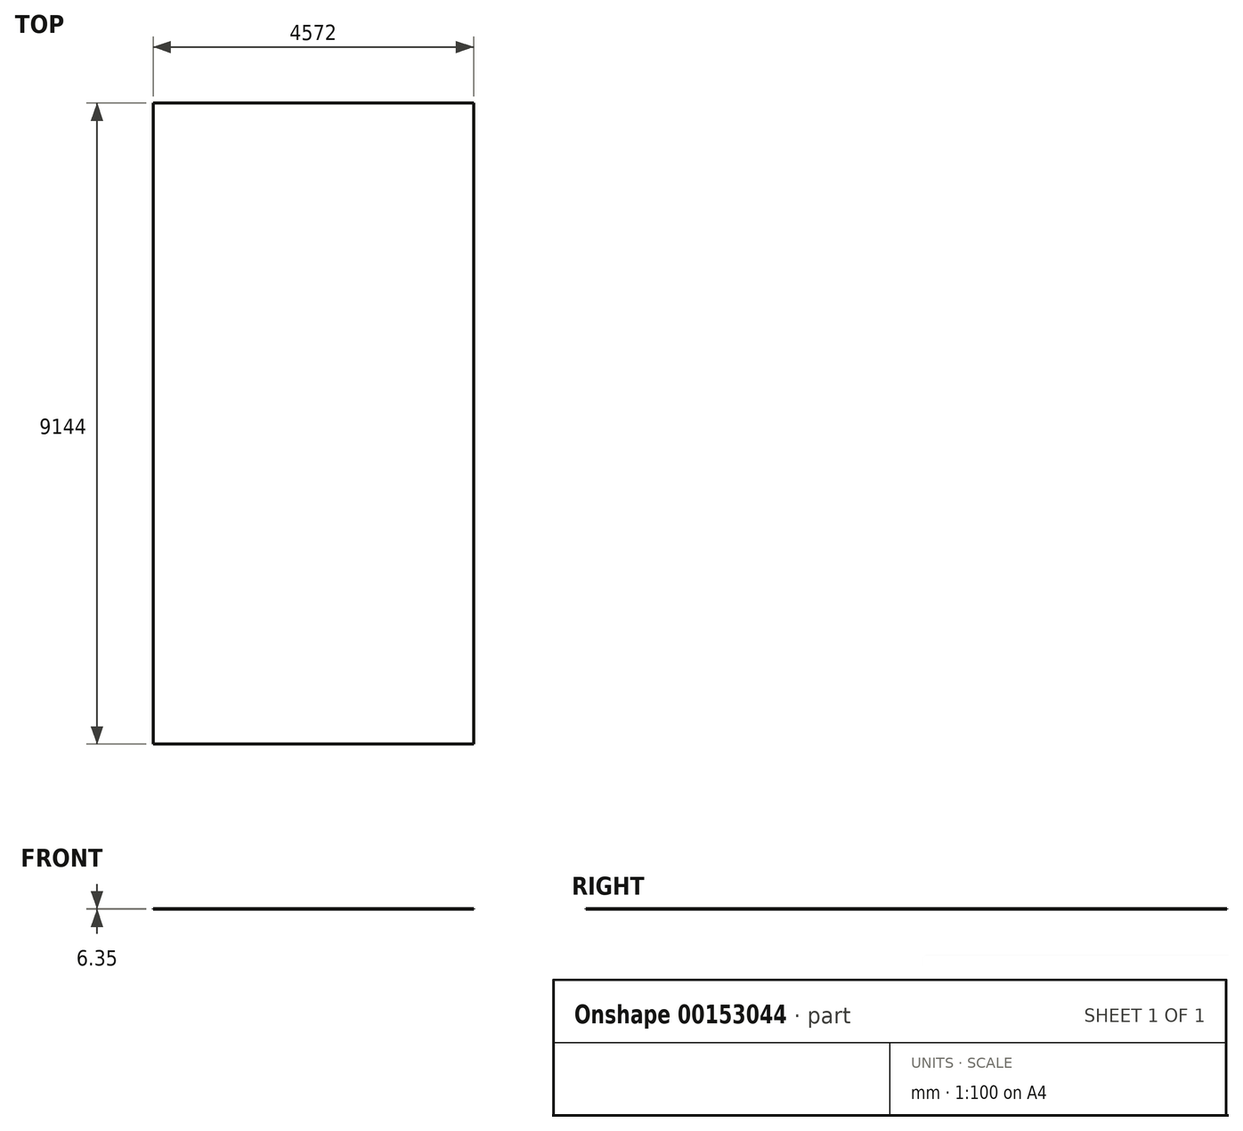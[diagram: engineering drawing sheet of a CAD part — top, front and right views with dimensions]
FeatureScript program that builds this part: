
annotation { "Feature Type Name" : "Feature", "Feature Type Description" : "" }
export const myFeature = defineFeature(function(context is Context, id is Id, definition is map)
    precondition{}
    {
        {
            var Q0;
            Q0=qCreatedBy(makeId("Top.planeOp"),FACE);
            var sketch = newSketch(context, id + "F0", { "sketchPlane" : qUnion([Q0])});
            skLineSegment(sketch, "E0.bottom", {"start": v(0, 0) * mm, "end": v(-4572, 0) * mm});
            skLineSegment(sketch, "E0.top", {"start": v(0, -9144) * mm, "end": v(-4572, -9144) * mm});
            skLineSegment(sketch, "E0.left", {"start": v(0, 0) * mm, "end": v(0, -9144) * mm});
            skLineSegment(sketch, "E0.right", {"start": v(-4572, 0) * mm, "end": v(-4572, -9144) * mm});
            skSolve(sketch);
        }
        {
            var Q0;
            Q0 = qSketchRegion(id + "F0", true);
            extrude(context, id + "F1", {"entities" : qUnion([Q0]), "depth" : 6.35 * mm});
        }
    });
